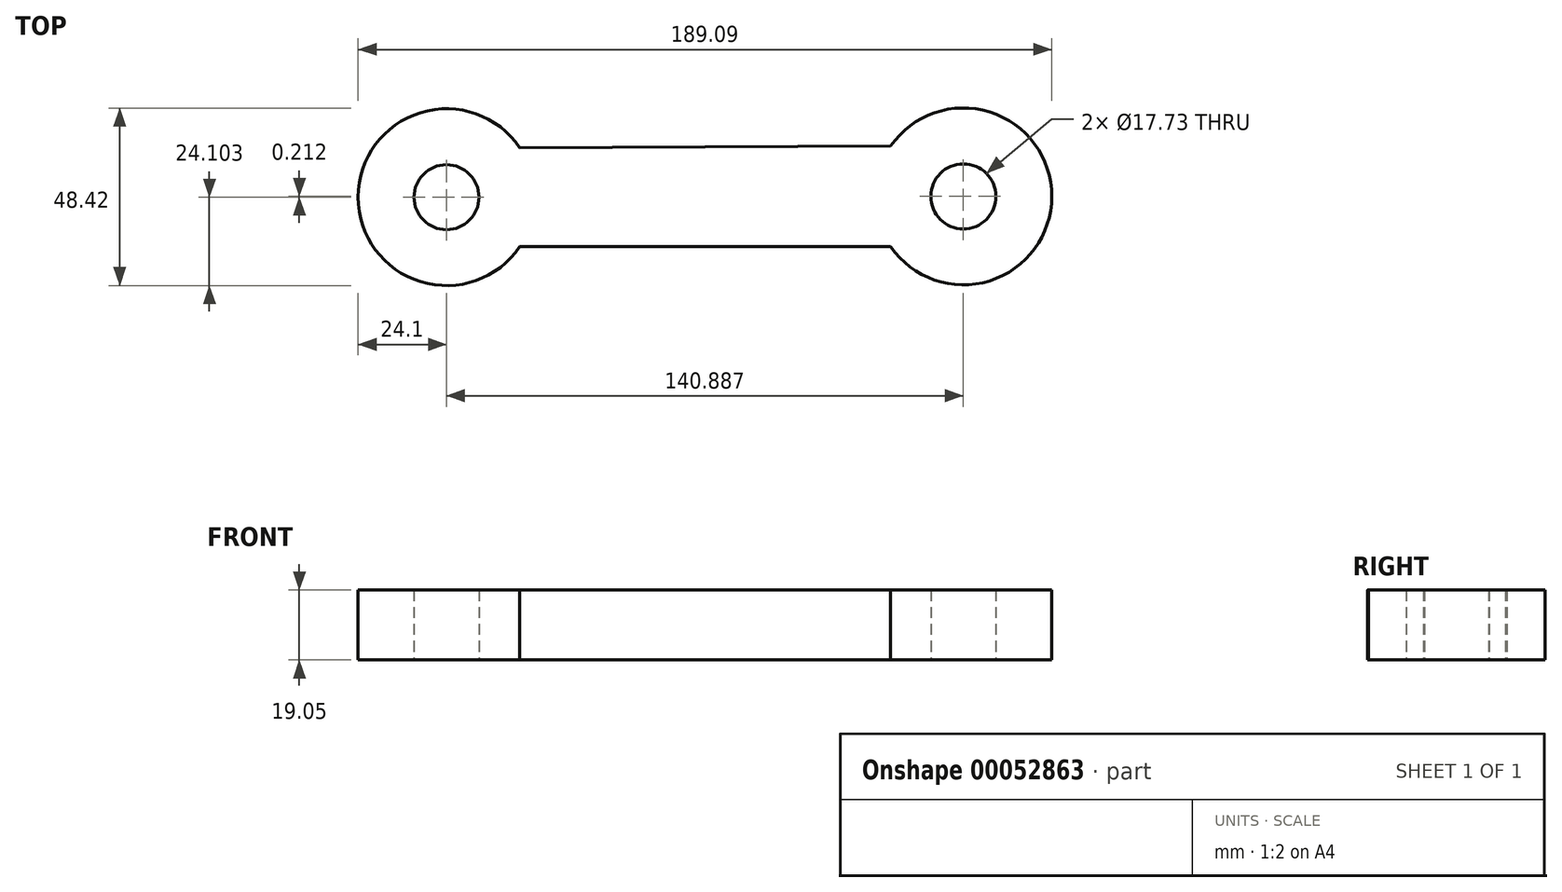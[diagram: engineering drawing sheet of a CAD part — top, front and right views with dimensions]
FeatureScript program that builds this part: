
annotation { "Feature Type Name" : "Feature", "Feature Type Description" : "" }
export const myFeature = defineFeature(function(context is Context, id is Id, definition is map)
    precondition{}
    {
        {
            var Q0;
            Q0=qCreatedBy(makeId("Top.planeOp"),FACE);
            var sketch = newSketch(context, id + "F0", { "sketchPlane" : qUnion([Q0])});
            skArc(sketch, "E0", {"start": v(-85.72, 19.83) * mm, "mid": v(-129.8, 6.34) * mm, "end": v(-85.72, -7.14) * mm});
            skLineSegment(sketch, "E1", {"start": v(-85.72, 19.83) * mm, "end": v(-85.72, 19.83) * mm});
            skLineSegment(sketch, "E2", {"start": v(-85.72, -7.14) * mm, "end": v(15.36, -7.14) * mm});
            skArc(sketch, "E3", {"start": v(15.36, -7.14) * mm, "mid": v(59.3, 6.56) * mm, "end": v(15.36, 20.25) * mm});
            skLineSegment(sketch, "E4", {"start": v(15.36, -7.14) * mm, "end": v(15.36, -7.14) * mm});
            skLineSegment(sketch, "E5", {"start": v(-85.72, 19.83) * mm, "end": v(15.36, 20.25) * mm});
            skSolve(sketch);
        }
        {
            var Q0;
            Q0 = qSketchRegion(id + "F0", true);
            extrude(context, id + "F1", {"entities" : qUnion([Q0]), "depth" : 19.05 * mm});
        }
        {
            var Q0;
            Q0=makeQuery(id+"F1.opExtrude","CAP_FACE",FACE,{"disambiguationData":[OSD([sQuery(id+"F0.wireOp",EDGE,"E0"),sQuery(id+"F0.wireOp",EDGE,"E2"),sQuery(id+"F0.wireOp",EDGE,"E3"),sQuery(id+"F0.wireOp",EDGE,"E5")])],"isStart":false});
            var Q1;
            Q1=makeQuery(id+"F1.opExtrude","CAP_FACE",FACE,{"disambiguationData":[OSD([sQuery(id+"F0.wireOp",EDGE,"E0"),sQuery(id+"F0.wireOp",EDGE,"E2"),sQuery(id+"F0.wireOp",EDGE,"E3"),sQuery(id+"F0.wireOp",EDGE,"E5")])],"isStart":true});
            shell(context, id + "F2", {"entities" : qUnion([Q0, Q1]), "thickness" : 15.24 * mm});
        }
    });
